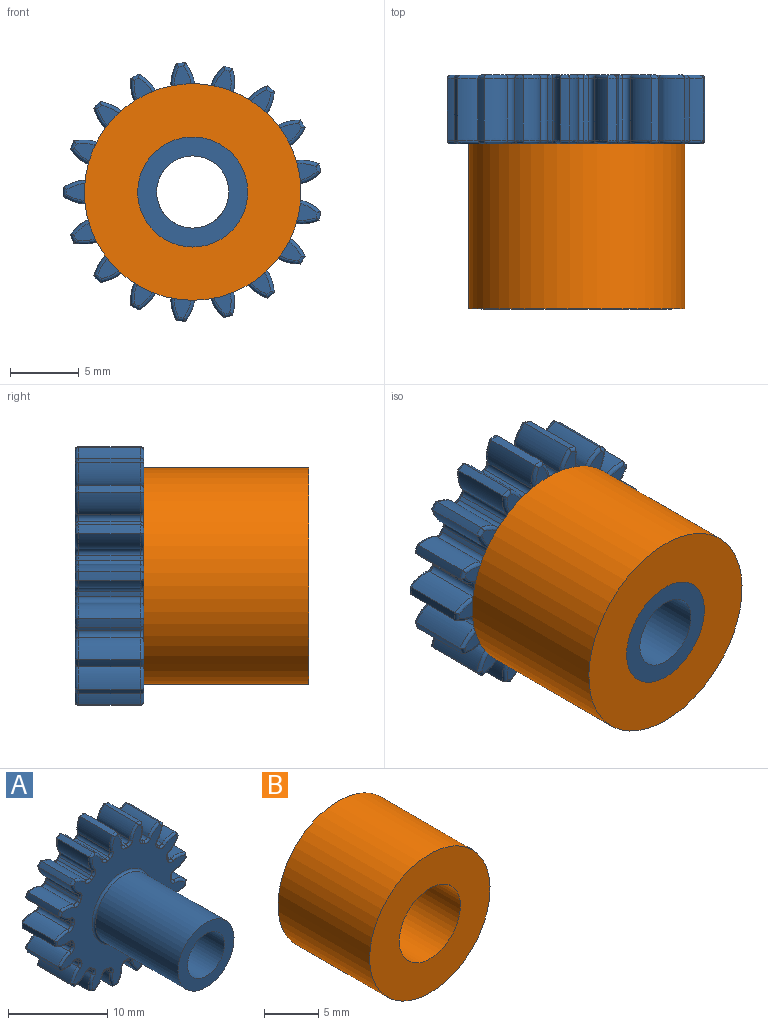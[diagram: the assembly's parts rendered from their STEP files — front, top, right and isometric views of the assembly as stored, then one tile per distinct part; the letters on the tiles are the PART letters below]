
ASSEMBLY  parts=2 mates=1
PART A: 313 faces, bbox 19.3x17x19.3 mm
  f0: cylinder r=9.42mm len=4.5mm, axis (0,1,0), area 3mm2, adj f65,f102,f161,f263
  f1: cylinder r=9.42mm len=4.5mm, axis (0,1,0), area 3mm2, adj f97,f100,f173,f275
  f2: cylinder r=9.42mm len=4.5mm, axis (0,1,0), area 3mm2, adj f85,f92,f197,f299
  f3: cylinder r=9.42mm len=4.5mm, axis (0,1,0), area 3mm2, adj f87,f95,f185,f287
  f4: cylinder r=9.42mm len=4.5mm, axis (0,1,0), area 3mm2, adj f45,f82,f113,f215
  f5: cylinder r=9.42mm len=4.5mm, axis (0,1,0), area 3mm2, adj f77,f80,f125,f227
  f6: cylinder r=9.42mm len=4.5mm, axis (0,1,0), area 3mm2, adj f72,f75,f137,f239
  f7: cylinder r=9.42mm len=4.5mm, axis (0,1,0), area 3mm2, adj f67,f70,f149,f251
  f8: cylinder r=9.42mm len=4.5mm, axis (0,1,0), area 3mm2, adj f25,f62,f150,f252
  f9: cylinder r=9.42mm len=4.5mm, axis (0,1,0), area 3mm2, adj f57,f60,f138,f240
  f10: cylinder r=9.42mm len=4.5mm, axis (0,1,0), area 3mm2, adj f52,f55,f126,f228
  f11: cylinder r=9.42mm len=4.5mm, axis (0,1,0), area 3mm2, adj f47,f50,f114,f216
  f12: cylinder r=9.42mm len=4.5mm, axis (0,1,0), area 3mm2, adj f35,f42,f186,f288
  f13: cylinder r=9.42mm len=4.5mm, axis (0,1,0), area 3mm2, adj f20,f37,f198,f300
  f14: cylinder r=9.42mm len=4.5mm, axis (0,1,0), area 3mm2, adj f32,f40,f174,f276
  f15: cylinder r=9.42mm len=4.5mm, axis (0,1,0), area 3mm2, adj f27,f30,f162,f264
  f16: plane 18.29x18.21mm, normal (0,-1,0), area 134.6mm2, adj f107,f108,f109,f110,f111,f112,f113,f114
  f17: cylinder r=2.62mm len=16.75mm, axis (0,1,0), area 276.3mm2, adj f106,f312
  f18: cylinder r=9.42mm len=4.5mm, axis (0,1,0), area 3mm2, adj f22,f90,f209,f311
  f19: plane 18.29x18.21mm, normal (0,1,0), area 165.4mm2, adj f210,f211,f212,f213,f214,f215,f216,f217
  f20: extruded ~4.5x1.76mm, area 9mm2, adj f13,f23,f200,f302
  f21: cylinder r=7.19mm len=4.5mm, axis (0,1,0), area 1.6mm2, adj f23,f24,f204,f306
  f22: extruded ~4.5x1.76mm, area 9mm2, adj f18,f24,f208,f310
  f23: cylinder r=0.4mm len=4.5mm, axis (0,1,0), area 2.7mm2, adj f20,f21,f202,f304
  f24: cylinder r=0.4mm len=4.5mm, axis (0,1,0), area 2.7mm2, adj f21,f22,f206,f308
  f25: extruded ~4.5x1.82mm, area 9mm2, adj f8,f28,f152,f254
  f26: cylinder r=7.19mm len=4.5mm, axis (0,1,0), area 1.6mm2, adj f28,f29,f156,f258
  f27: extruded ~4.5x1.67mm, area 9mm2, adj f15,f29,f160,f262
  f28: cylinder r=0.4mm len=4.5mm, axis (0,1,0), area 2.7mm2, adj f25,f26,f154,f256
  f29: cylinder r=0.4mm len=4.5mm, axis (0,1,0), area 2.7mm2, adj f26,f27,f158,f260
  f30: extruded ~4.5x1.94mm, area 9mm2, adj f15,f33,f164,f266
  f31: cylinder r=7.19mm len=4.5mm, axis (0,1,0), area 1.6mm2, adj f33,f34,f168,f270
  f32: extruded ~4.5x1.51mm, area 9mm2, adj f14,f34,f172,f274
  f33: cylinder r=0.4mm len=4.5mm, axis (0,1,0), area 2.7mm2, adj f30,f31,f166,f268
  f34: cylinder r=0.4mm len=4.5mm, axis (0,1,0), area 2.7mm2, adj f31,f32,f170,f272
  f35: extruded ~4.5x1.39mm, area 9mm2, adj f12,f38,f188,f290
  f36: cylinder r=7.19mm len=4.5mm, axis (0,1,0), area 1.6mm2, adj f38,f39,f192,f294
  f37: extruded ~4.5x1.93mm, area 9mm2, adj f13,f39,f196,f298
  f38: cylinder r=0.4mm len=4.5mm, axis (0,1,0), area 2.7mm2, adj f35,f36,f190,f292
  f39: cylinder r=0.4mm len=4.5mm, axis (0,1,0), area 2.7mm2, adj f36,f37,f194,f296
  f40: extruded ~4.5x1.79mm, area 9mm2, adj f14,f43,f176,f278
  f41: cylinder r=7.19mm len=4.5mm, axis (0,1,0), area 1.6mm2, adj f43,f44,f180,f282
  f42: extruded ~4.5x1.85mm, area 9mm2, adj f12,f44,f184,f286
  f43: cylinder r=0.4mm len=4.5mm, axis (0,1,0), area 2.7mm2, adj f40,f41,f178,f280
  f44: cylinder r=0.4mm len=4.5mm, axis (0,1,0), area 2.7mm2, adj f41,f42,f182,f284
  f45: extruded ~4.5x1.88mm, area 9mm2, adj f4,f48,f111,f213
  f46: cylinder r=7.19mm len=4.5mm, axis (0,1,0), area 1.6mm2, adj f48,f49,f108,f210
  f47: extruded ~4.5x1.58mm, area 9mm2, adj f11,f49,f112,f214
  f48: cylinder r=0.4mm len=4.5mm, axis (0,1,0), area 2.7mm2, adj f45,f46,f109,f211
  f49: cylinder r=0.4mm len=4.5mm, axis (0,1,0), area 2.7mm2, adj f46,f47,f110,f212
  f50: extruded ~4.5x1.92mm, area 9mm2, adj f11,f53,f116,f218
  f51: cylinder r=7.19mm len=4.5mm, axis (0,1,0), area 1.6mm2, adj f53,f54,f120,f222
  f52: extruded ~4.5x1.62mm, area 9mm2, adj f10,f54,f124,f226
  f53: cylinder r=0.4mm len=4.5mm, axis (0,1,0), area 2.7mm2, adj f50,f51,f118,f220
  f54: cylinder r=0.4mm len=4.5mm, axis (0,1,0), area 2.7mm2, adj f51,f52,f122,f224
  f55: extruded ~4.5x1.71mm, area 9mm2, adj f10,f58,f128,f230
  f56: cylinder r=7.19mm len=4.5mm, axis (0,1,0), area 1.6mm2, adj f58,f59,f132,f234
  f57: extruded ~4.5x1.89mm, area 9mm2, adj f9,f59,f136,f238
  f58: cylinder r=0.4mm len=4.5mm, axis (0,1,0), area 2.7mm2, adj f55,f56,f130,f232
  f59: cylinder r=0.4mm len=4.5mm, axis (0,1,0), area 2.7mm2, adj f56,f57,f134,f236
  f60: extruded ~4.5x1.47mm, area 9mm2, adj f9,f63,f140,f242
  f61: cylinder r=7.19mm len=4.5mm, axis (0,1,0), area 1.6mm2, adj f63,f64,f144,f246
  f62: extruded ~4.5x1.91mm, area 9mm2, adj f8,f64,f148,f250
  f63: cylinder r=0.4mm len=4.5mm, axis (0,1,0), area 2.7mm2, adj f60,f61,f142,f244
  f64: cylinder r=0.4mm len=4.5mm, axis (0,1,0), area 2.7mm2, adj f61,f62,f146,f248
  f65: extruded ~4.5x1.91mm, area 9mm2, adj f0,f68,f159,f261
  f66: cylinder r=7.19mm len=4.5mm, axis (0,1,0), area 1.6mm2, adj f68,f69,f155,f257
  f67: extruded ~4.5x1.47mm, area 9mm2, adj f7,f69,f151,f253
  f68: cylinder r=0.4mm len=4.5mm, axis (0,1,0), area 2.7mm2, adj f65,f66,f157,f259
  f69: cylinder r=0.4mm len=4.5mm, axis (0,1,0), area 2.7mm2, adj f66,f67,f153,f255
  f70: extruded ~4.5x1.89mm, area 9mm2, adj f7,f73,f147,f249
  f71: cylinder r=7.19mm len=4.5mm, axis (0,1,0), area 1.6mm2, adj f73,f74,f143,f245
  f72: extruded ~4.5x1.71mm, area 9mm2, adj f6,f74,f139,f241
  f73: cylinder r=0.4mm len=4.5mm, axis (0,1,0), area 2.7mm2, adj f70,f71,f145,f247
  f74: cylinder r=0.4mm len=4.5mm, axis (0,1,0), area 2.7mm2, adj f71,f72,f141,f243
  f75: extruded ~4.5x1.62mm, area 9mm2, adj f6,f78,f135,f237
  f76: cylinder r=7.19mm len=4.5mm, axis (0,1,0), area 1.6mm2, adj f78,f79,f131,f233
  f77: extruded ~4.5x1.92mm, area 9mm2, adj f5,f79,f127,f229
  f78: cylinder r=0.4mm len=4.5mm, axis (0,1,0), area 2.7mm2, adj f75,f76,f133,f235
  f79: cylinder r=0.4mm len=4.5mm, axis (0,1,0), area 2.7mm2, adj f76,f77,f129,f231
  f80: extruded ~4.5x1.58mm, area 9mm2, adj f5,f83,f123,f225
  f81: cylinder r=7.19mm len=4.5mm, axis (0,1,0), area 1.6mm2, adj f83,f84,f119,f221
  f82: extruded ~4.5x1.88mm, area 9mm2, adj f4,f84,f115,f217
  f83: cylinder r=0.4mm len=4.5mm, axis (0,1,0), area 2.7mm2, adj f80,f81,f121,f223
  f84: cylinder r=0.4mm len=4.5mm, axis (0,1,0), area 2.7mm2, adj f81,f82,f117,f219
  f85: extruded ~4.5x1.85mm, area 9mm2, adj f2,f88,f195,f297
  f86: cylinder r=7.19mm len=4.5mm, axis (0,1,0), area 1.6mm2, adj f88,f89,f191,f293
  f87: extruded ~4.5x1.79mm, area 9mm2, adj f3,f89,f187,f289
  f88: cylinder r=0.4mm len=4.5mm, axis (0,1,0), area 2.7mm2, adj f85,f86,f193,f295
  f89: cylinder r=0.4mm len=4.5mm, axis (0,1,0), area 2.7mm2, adj f86,f87,f189,f291
  f90: extruded ~4.5x1.93mm, area 9mm2, adj f18,f93,f207,f309
  f91: cylinder r=7.19mm len=4.5mm, axis (0,1,0), area 1.6mm2, adj f93,f94,f203,f305
  f92: extruded ~4.5x1.39mm, area 9mm2, adj f2,f94,f199,f301
  f93: cylinder r=0.4mm len=4.5mm, axis (0,1,0), area 2.7mm2, adj f90,f91,f205,f307
  f94: cylinder r=0.4mm len=4.5mm, axis (0,1,0), area 2.7mm2, adj f91,f92,f201,f303
  f95: extruded ~4.5x1.51mm, area 9mm2, adj f3,f98,f183,f285
  f96: cylinder r=7.19mm len=4.5mm, axis (0,1,0), area 1.6mm2, adj f98,f99,f179,f281
  f97: extruded ~4.5x1.94mm, area 9mm2, adj f1,f99,f175,f277
  f98: cylinder r=0.4mm len=4.5mm, axis (0,1,0), area 2.7mm2, adj f95,f96,f181,f283
  f99: cylinder r=0.4mm len=4.5mm, axis (0,1,0), area 2.7mm2, adj f96,f97,f177,f279
  f100: extruded ~4.5x1.67mm, area 9mm2, adj f1,f103,f171,f273
  f101: cylinder r=7.19mm len=4.5mm, axis (0,1,0), area 1.6mm2, adj f103,f104,f167,f269
  f102: extruded ~4.5x1.82mm, area 9mm2, adj f0,f104,f163,f265
  f103: cylinder r=0.4mm len=4.5mm, axis (0,1,0), area 2.7mm2, adj f100,f101,f169,f271
  f104: cylinder r=0.4mm len=4.5mm, axis (0,1,0), area 2.7mm2, adj f101,f102,f165,f267
  f105: cylinder r=4mm len=11.75mm, axis (0,1,0), area 295.3mm2, adj f106,f107
  f106: plane 8x8mm, normal (0,-1,0), area 28.6mm2, adj f17,f105
  f107: torus R=4.25mm, axis (0,-1,0), area 10.1mm2, adj f16,f105
  f108: torus R=6.94mm, axis (0,-1,0), area 0.1mm2, adj f16,f46,f109,f110
  f109: torus R=0.65mm, axis (0,-1,0), area 0.3mm2, adj f16,f48,f108,f111
  f110: torus R=0.65mm, axis (0,-1,0), area 0.3mm2, adj f16,f49,f108,f112
  f111: bspline ~3.83x0.9mm, area 0.7mm2, adj f16,f45,f109,f113
  f112: bspline ~2.24x1.65mm, area 0.7mm2, adj f16,f47,f110,f114
  f113: torus R=9.17mm, axis (0,-1,0), area 0.2mm2, adj f4,f16,f111,f115
  f114: torus R=9.17mm, axis (0,-1,0), area 0.2mm2, adj f11,f16,f112,f116
  f115: bspline ~3.83x0.9mm, area 0.7mm2, adj f16,f82,f113,f117
  f116: bspline ~3.73x1.28mm, area 0.7mm2, adj f16,f50,f114,f118
  f117: torus R=0.65mm, axis (0,-1,0), area 0.3mm2, adj f16,f84,f115,f119
  f118: torus R=0.65mm, axis (0,-1,0), area 0.3mm2, adj f16,f53,f116,f120
  f119: torus R=6.94mm, axis (0,-1,0), area 0.1mm2, adj f16,f81,f117,f121
  f120: torus R=6.94mm, axis (0,-1,0), area 0.1mm2, adj f16,f51,f118,f122
  f121: torus R=0.65mm, axis (0,-1,0), area 0.3mm2, adj f16,f83,f119,f123
  f122: torus R=0.65mm, axis (0,-1,0), area 0.3mm2, adj f16,f54,f120,f124
  f123: bspline ~3.43x1.97mm, area 0.7mm2, adj f16,f80,f121,f125
  f124: bspline ~2.99x2.65mm, area 0.7mm2, adj f16,f52,f122,f126
  f125: torus R=9.17mm, axis (0,-1,0), area 0.2mm2, adj f5,f16,f123,f127
  f126: torus R=9.17mm, axis (0,-1,0), area 0.2mm2, adj f10,f16,f124,f128
  f127: bspline ~3.73x1.28mm, area 0.7mm2, adj f16,f77,f125,f129
  f128: bspline ~3.19x2.39mm, area 0.7mm2, adj f16,f55,f126,f130
  f129: torus R=0.65mm, axis (0,-1,0), area 0.3mm2, adj f16,f79,f127,f131
  f130: torus R=0.65mm, axis (0,-1,0), area 0.3mm2, adj f16,f58,f128,f132
  f131: torus R=6.94mm, axis (0,-1,0), area 0.1mm2, adj f16,f76,f129,f133
  f132: torus R=6.94mm, axis (0,-1,0), area 0.1mm2, adj f16,f56,f130,f134
  f133: torus R=0.65mm, axis (0,-1,0), area 0.3mm2, adj f16,f78,f131,f135
  f134: torus R=0.65mm, axis (0,-1,0), area 0.3mm2, adj f16,f59,f132,f136
  f135: bspline ~2.99x2.65mm, area 0.7mm2, adj f16,f75,f133,f137
  f136: bspline ~3.62x1.52mm, area 0.7mm2, adj f16,f57,f134,f138
  f137: torus R=9.17mm, axis (0,-1,0), area 0.2mm2, adj f6,f16,f135,f139
  f138: torus R=9.17mm, axis (0,-1,0), area 0.2mm2, adj f9,f16,f136,f140
  f139: bspline ~3.19x2.39mm, area 0.7mm2, adj f16,f72,f137,f141
  f140: bspline ~3.27x2.25mm, area 0.7mm2, adj f16,f60,f138,f142
  f141: torus R=0.65mm, axis (0,-1,0), area 0.3mm2, adj f16,f74,f139,f143
  f142: torus R=0.65mm, axis (0,-1,0), area 0.3mm2, adj f16,f63,f140,f144
  f143: torus R=6.94mm, axis (0,-1,0), area 0.1mm2, adj f16,f71,f141,f145
  f144: torus R=6.94mm, axis (0,-1,0), area 0.1mm2, adj f16,f61,f142,f146
  f145: torus R=0.65mm, axis (0,-1,0), area 0.3mm2, adj f16,f73,f143,f147
  f146: torus R=0.65mm, axis (0,-1,0), area 0.3mm2, adj f16,f64,f144,f148
  f147: bspline ~3.62x1.52mm, area 0.7mm2, adj f16,f70,f145,f149
  f148: bspline ~3.85x0.75mm, area 0.7mm2, adj f16,f62,f146,f150
  f149: torus R=9.17mm, axis (0,-1,0), area 0.2mm2, adj f7,f16,f147,f151
  f150: torus R=9.17mm, axis (0,-1,0), area 0.2mm2, adj f8,f16,f148,f152
  f151: bspline ~3.27x2.25mm, area 0.7mm2, adj f16,f67,f149,f153
  f152: bspline ~3.77x1.06mm, area 0.7mm2, adj f16,f25,f150,f154
  f153: torus R=0.65mm, axis (0,-1,0), area 0.3mm2, adj f16,f69,f151,f155
  f154: torus R=0.65mm, axis (0,-1,0), area 0.3mm2, adj f16,f28,f152,f156
  f155: torus R=6.94mm, axis (0,-1,0), area 0.1mm2, adj f16,f66,f153,f157
  f156: torus R=6.94mm, axis (0,-1,0), area 0.1mm2, adj f16,f26,f154,f158
  f157: torus R=0.65mm, axis (0,-1,0), area 0.3mm2, adj f16,f68,f155,f159
  f158: torus R=0.65mm, axis (0,-1,0), area 0.3mm2, adj f16,f29,f156,f160
  f159: bspline ~3.85x0.75mm, area 0.7mm2, adj f16,f65,f157,f161
  f160: bspline ~3.61x1.67mm, area 0.7mm2, adj f16,f27,f158,f162
  f161: torus R=9.17mm, axis (0,-1,0), area 0.2mm2, adj f0,f16,f159,f163
  f162: torus R=9.17mm, axis (0,-1,0), area 0.2mm2, adj f15,f16,f160,f164
  f163: bspline ~3.77x1.06mm, area 0.7mm2, adj f16,f102,f161,f165
  f164: bspline ~3.8x1.06mm, area 0.7mm2, adj f16,f30,f162,f166
  f165: torus R=0.65mm, axis (0,-1,0), area 0.3mm2, adj f16,f104,f163,f167
  f166: torus R=0.65mm, axis (0,-1,0), area 0.3mm2, adj f16,f33,f164,f168
  f167: torus R=6.94mm, axis (0,-1,0), area 0.1mm2, adj f16,f101,f165,f169
  f168: torus R=6.94mm, axis (0,-1,0), area 0.1mm2, adj f16,f31,f166,f170
  f169: torus R=0.65mm, axis (0,-1,0), area 0.3mm2, adj f16,f103,f167,f171
  f170: torus R=0.65mm, axis (0,-1,0), area 0.3mm2, adj f16,f34,f168,f172
  f171: bspline ~3.61x1.67mm, area 0.7mm2, adj f16,f100,f169,f173
  f172: bspline ~2.87x2.76mm, area 0.7mm2, adj f16,f32,f170,f174
  f173: torus R=9.17mm, axis (0,-1,0), area 0.2mm2, adj f1,f16,f171,f175
  f174: torus R=9.17mm, axis (0,-1,0), area 0.2mm2, adj f14,f16,f172,f176
  f175: bspline ~3.8x1.06mm, area 0.7mm2, adj f16,f97,f173,f177
  f176: bspline ~3.35x2.1mm, area 0.7mm2, adj f16,f40,f174,f178
  f177: torus R=0.65mm, axis (0,-1,0), area 0.3mm2, adj f16,f99,f175,f179
  f178: torus R=0.65mm, axis (0,-1,0), area 0.3mm2, adj f16,f43,f176,f180
  f179: torus R=6.94mm, axis (0,-1,0), area 0.1mm2, adj f16,f96,f177,f181
  f180: torus R=6.94mm, axis (0,-1,0), area 0.1mm2, adj f16,f41,f178,f182
  f181: torus R=0.65mm, axis (0,-1,0), area 0.3mm2, adj f16,f98,f179,f183
  f182: torus R=0.65mm, axis (0,-1,0), area 0.3mm2, adj f16,f44,f180,f184
  f183: bspline ~2.87x2.76mm, area 0.7mm2, adj f16,f95,f181,f185
  f184: bspline ~3.48x1.79mm, area 0.7mm2, adj f16,f42,f182,f186
  f185: torus R=9.17mm, axis (0,-1,0), area 0.2mm2, adj f3,f16,f183,f187
  f186: torus R=9.17mm, axis (0,-1,0), area 0.2mm2, adj f12,f16,f184,f188
  f187: bspline ~3.35x2.1mm, area 0.7mm2, adj f16,f87,f185,f189
  f188: bspline ~3.08x2.51mm, area 0.7mm2, adj f16,f35,f186,f190
  f189: torus R=0.65mm, axis (0,-1,0), area 0.3mm2, adj f16,f89,f187,f191
  f190: torus R=0.65mm, axis (0,-1,0), area 0.3mm2, adj f16,f38,f188,f192
  f191: torus R=6.94mm, axis (0,-1,0), area 0.1mm2, adj f16,f86,f189,f193
  f192: torus R=6.94mm, axis (0,-1,0), area 0.1mm2, adj f16,f36,f190,f194
  f193: torus R=0.65mm, axis (0,-1,0), area 0.3mm2, adj f16,f88,f191,f195
  f194: torus R=0.65mm, axis (0,-1,0), area 0.3mm2, adj f16,f39,f192,f196
  f195: bspline ~3.48x1.79mm, area 0.7mm2, adj f16,f85,f193,f197
  f196: bspline ~3.85x0.85mm, area 0.7mm2, adj f16,f37,f194,f198
  f197: torus R=9.17mm, axis (0,-1,0), area 0.2mm2, adj f2,f16,f195,f199
  f198: torus R=9.17mm, axis (0,-1,0), area 0.2mm2, adj f13,f16,f196,f200
  f199: bspline ~3.08x2.51mm, area 0.7mm2, adj f16,f92,f197,f201
  f200: bspline ~3.71x1.35mm, area 0.7mm2, adj f16,f20,f198,f202
  f201: torus R=0.65mm, axis (0,-1,0), area 0.3mm2, adj f16,f94,f199,f203
  f202: torus R=0.65mm, axis (0,-1,0), area 0.3mm2, adj f16,f23,f200,f204
  f203: torus R=6.94mm, axis (0,-1,0), area 0.1mm2, adj f16,f91,f201,f205
  f204: torus R=6.94mm, axis (0,-1,0), area 0.1mm2, adj f16,f21,f202,f206
  f205: torus R=0.65mm, axis (0,-1,0), area 0.3mm2, adj f16,f93,f203,f207
  f206: torus R=0.65mm, axis (0,-1,0), area 0.3mm2, adj f16,f24,f204,f208
  f207: bspline ~3.85x0.85mm, area 0.7mm2, adj f16,f90,f205,f209
  f208: bspline ~3.71x1.35mm, area 0.7mm2, adj f16,f22,f206,f209
  f209: torus R=9.17mm, axis (0,-1,0), area 0.2mm2, adj f16,f18,f207,f208
  f210: torus R=6.94mm, axis (0,-1,0), area 0.1mm2, adj f19,f46,f211,f212
  f211: torus R=0.65mm, axis (0,-1,0), area 0.3mm2, adj f19,f48,f210,f213
  f212: torus R=0.65mm, axis (0,-1,0), area 0.3mm2, adj f19,f49,f210,f214
  f213: bspline ~3.83x0.9mm, area 0.7mm2, adj f19,f45,f211,f215
  f214: bspline ~3.43x1.97mm, area 0.7mm2, adj f19,f47,f212,f216
  f215: torus R=9.17mm, axis (0,-1,0), area 0.2mm2, adj f4,f19,f213,f217
  f216: torus R=9.17mm, axis (0,-1,0), area 0.2mm2, adj f11,f19,f214,f218
  f217: bspline ~3.83x0.9mm, area 0.7mm2, adj f19,f82,f215,f219
  f218: bspline ~3.73x1.28mm, area 0.7mm2, adj f19,f50,f216,f220
  f219: torus R=0.65mm, axis (0,-1,0), area 0.3mm2, adj f19,f84,f217,f221
  f220: torus R=0.65mm, axis (0,-1,0), area 0.3mm2, adj f19,f53,f218,f222
  f221: torus R=6.94mm, axis (0,-1,0), area 0.1mm2, adj f19,f81,f219,f223
  f222: torus R=6.94mm, axis (0,-1,0), area 0.1mm2, adj f19,f51,f220,f224
  f223: torus R=0.65mm, axis (0,-1,0), area 0.3mm2, adj f19,f83,f221,f225
  f224: torus R=0.65mm, axis (0,-1,0), area 0.3mm2, adj f19,f54,f222,f226
  f225: bspline ~3.43x1.97mm, area 0.7mm2, adj f19,f80,f223,f227
  f226: bspline ~2.99x2.65mm, area 0.7mm2, adj f19,f52,f224,f228
  f227: torus R=9.17mm, axis (0,-1,0), area 0.2mm2, adj f5,f19,f225,f229
  f228: torus R=9.17mm, axis (0,-1,0), area 0.2mm2, adj f10,f19,f226,f230
  f229: bspline ~3.73x1.28mm, area 0.7mm2, adj f19,f77,f227,f231
  f230: bspline ~3.19x2.39mm, area 0.7mm2, adj f19,f55,f228,f232
  f231: torus R=0.65mm, axis (0,-1,0), area 0.3mm2, adj f19,f79,f229,f233
  f232: torus R=0.65mm, axis (0,-1,0), area 0.3mm2, adj f19,f58,f230,f234
  f233: torus R=6.94mm, axis (0,-1,0), area 0.1mm2, adj f19,f76,f231,f235
  f234: torus R=6.94mm, axis (0,-1,0), area 0.1mm2, adj f19,f56,f232,f236
  f235: torus R=0.65mm, axis (0,-1,0), area 0.3mm2, adj f19,f78,f233,f237
  f236: torus R=0.65mm, axis (0,-1,0), area 0.3mm2, adj f19,f59,f234,f238
  f237: bspline ~2.99x2.65mm, area 0.7mm2, adj f19,f75,f235,f239
  f238: bspline ~3.62x1.52mm, area 0.7mm2, adj f19,f57,f236,f240
  f239: torus R=9.17mm, axis (0,-1,0), area 0.2mm2, adj f6,f19,f237,f241
  f240: torus R=9.17mm, axis (0,-1,0), area 0.2mm2, adj f9,f19,f238,f242
  f241: bspline ~3.19x2.39mm, area 0.7mm2, adj f19,f72,f239,f243
  f242: bspline ~3.27x2.25mm, area 0.7mm2, adj f19,f60,f240,f244
  f243: torus R=0.65mm, axis (0,-1,0), area 0.3mm2, adj f19,f74,f241,f245
  f244: torus R=0.65mm, axis (0,-1,0), area 0.3mm2, adj f19,f63,f242,f246
  f245: torus R=6.94mm, axis (0,-1,0), area 0.1mm2, adj f19,f71,f243,f247
  f246: torus R=6.94mm, axis (0,-1,0), area 0.1mm2, adj f19,f61,f244,f248
  f247: torus R=0.65mm, axis (0,-1,0), area 0.3mm2, adj f19,f73,f245,f249
  f248: torus R=0.65mm, axis (0,-1,0), area 0.3mm2, adj f19,f64,f246,f250
  f249: bspline ~3.62x1.52mm, area 0.7mm2, adj f19,f70,f247,f251
  f250: bspline ~3.85x0.75mm, area 0.7mm2, adj f19,f62,f248,f252
  f251: torus R=9.17mm, axis (0,-1,0), area 0.2mm2, adj f7,f19,f249,f253
  f252: torus R=9.17mm, axis (0,-1,0), area 0.2mm2, adj f8,f19,f250,f254
  f253: bspline ~3.27x2.25mm, area 0.7mm2, adj f19,f67,f251,f255
  f254: bspline ~3.77x1.06mm, area 0.7mm2, adj f19,f25,f252,f256
  f255: torus R=0.65mm, axis (0,-1,0), area 0.3mm2, adj f19,f69,f253,f257
  f256: torus R=0.65mm, axis (0,-1,0), area 0.3mm2, adj f19,f28,f254,f258
  f257: torus R=6.94mm, axis (0,-1,0), area 0.1mm2, adj f19,f66,f255,f259
  f258: torus R=6.94mm, axis (0,-1,0), area 0.1mm2, adj f19,f26,f256,f260
  f259: torus R=0.65mm, axis (0,-1,0), area 0.3mm2, adj f19,f68,f257,f261
  f260: torus R=0.65mm, axis (0,-1,0), area 0.3mm2, adj f19,f29,f258,f262
  f261: bspline ~3.85x0.75mm, area 0.7mm2, adj f19,f65,f259,f263
  f262: bspline ~3.61x1.67mm, area 0.7mm2, adj f19,f27,f260,f264
  f263: torus R=9.17mm, axis (0,-1,0), area 0.2mm2, adj f0,f19,f261,f265
  f264: torus R=9.17mm, axis (0,-1,0), area 0.2mm2, adj f15,f19,f262,f266
  f265: bspline ~3.77x1.06mm, area 0.7mm2, adj f19,f102,f263,f267
  f266: bspline ~3.8x1.06mm, area 0.7mm2, adj f19,f30,f264,f268
  f267: torus R=0.65mm, axis (0,-1,0), area 0.3mm2, adj f19,f104,f265,f269
  f268: torus R=0.65mm, axis (0,-1,0), area 0.3mm2, adj f19,f33,f266,f270
  f269: torus R=6.94mm, axis (0,-1,0), area 0.1mm2, adj f19,f101,f267,f271
  f270: torus R=6.94mm, axis (0,-1,0), area 0.1mm2, adj f19,f31,f268,f272
  f271: torus R=0.65mm, axis (0,-1,0), area 0.3mm2, adj f19,f103,f269,f273
  f272: torus R=0.65mm, axis (0,-1,0), area 0.3mm2, adj f19,f34,f270,f274
  f273: bspline ~2.36x1.46mm, area 0.7mm2, adj f19,f100,f271,f275
  f274: bspline ~2.87x2.76mm, area 0.7mm2, adj f19,f32,f272,f276
  f275: torus R=9.17mm, axis (0,-1,0), area 0.2mm2, adj f1,f19,f273,f277
  f276: torus R=9.17mm, axis (0,-1,0), area 0.2mm2, adj f14,f19,f274,f278
  f277: bspline ~3.8x1.06mm, area 0.7mm2, adj f19,f97,f275,f279
  f278: bspline ~3.35x2.1mm, area 0.7mm2, adj f19,f40,f276,f280
  f279: torus R=0.65mm, axis (0,-1,0), area 0.3mm2, adj f19,f99,f277,f281
  f280: torus R=0.65mm, axis (0,-1,0), area 0.3mm2, adj f19,f43,f278,f282
  f281: torus R=6.94mm, axis (0,-1,0), area 0.1mm2, adj f19,f96,f279,f283
  f282: torus R=6.94mm, axis (0,-1,0), area 0.1mm2, adj f19,f41,f280,f284
  f283: torus R=0.65mm, axis (0,-1,0), area 0.3mm2, adj f19,f98,f281,f285
  f284: torus R=0.65mm, axis (0,-1,0), area 0.3mm2, adj f19,f44,f282,f286
  f285: bspline ~2.87x2.76mm, area 0.7mm2, adj f19,f95,f283,f287
  f286: bspline ~3.48x1.79mm, area 0.7mm2, adj f19,f42,f284,f288
  f287: torus R=9.17mm, axis (0,-1,0), area 0.2mm2, adj f3,f19,f285,f289
  f288: torus R=9.17mm, axis (0,-1,0), area 0.2mm2, adj f12,f19,f286,f290
  f289: bspline ~3.35x2.1mm, area 0.7mm2, adj f19,f87,f287,f291
  f290: bspline ~3.08x2.51mm, area 0.7mm2, adj f19,f35,f288,f292
  f291: torus R=0.65mm, axis (0,-1,0), area 0.3mm2, adj f19,f89,f289,f293
  f292: torus R=0.65mm, axis (0,-1,0), area 0.3mm2, adj f19,f38,f290,f294
  f293: torus R=6.94mm, axis (0,-1,0), area 0.1mm2, adj f19,f86,f291,f295
  f294: torus R=6.94mm, axis (0,-1,0), area 0.1mm2, adj f19,f36,f292,f296
  f295: torus R=0.65mm, axis (0,-1,0), area 0.3mm2, adj f19,f88,f293,f297
  f296: torus R=0.65mm, axis (0,-1,0), area 0.3mm2, adj f19,f39,f294,f298
  f297: bspline ~3.48x1.79mm, area 0.7mm2, adj f19,f85,f295,f299
  f298: bspline ~3.85x0.85mm, area 0.7mm2, adj f19,f37,f296,f300
  f299: torus R=9.17mm, axis (0,-1,0), area 0.2mm2, adj f2,f19,f297,f301
  f300: torus R=9.17mm, axis (0,-1,0), area 0.2mm2, adj f13,f19,f298,f302
  f301: bspline ~3.08x2.51mm, area 0.7mm2, adj f19,f92,f299,f303
  f302: bspline ~3.71x1.35mm, area 0.7mm2, adj f19,f20,f300,f304
  f303: torus R=0.65mm, axis (0,-1,0), area 0.3mm2, adj f19,f94,f301,f305
  f304: torus R=0.65mm, axis (0,-1,0), area 0.3mm2, adj f19,f23,f302,f306
  f305: torus R=6.94mm, axis (0,-1,0), area 0.1mm2, adj f19,f91,f303,f307
  f306: torus R=6.94mm, axis (0,-1,0), area 0.1mm2, adj f19,f21,f304,f308
  f307: torus R=0.65mm, axis (0,-1,0), area 0.3mm2, adj f19,f93,f305,f309
  f308: torus R=0.65mm, axis (0,-1,0), area 0.3mm2, adj f19,f24,f306,f310
  f309: bspline ~3.85x0.85mm, area 0.7mm2, adj f19,f90,f307,f311
  f310: bspline ~3.71x1.35mm, area 0.7mm2, adj f19,f22,f308,f311
  f311: torus R=9.17mm, axis (0,-1,0), area 0.2mm2, adj f18,f19,f309,f310
  f312: torus R=2.88mm, axis (0,-1,0), area 6.7mm2, adj f17,f19
PART B: 4 faces, bbox 15.8x12x15.8 mm
  f0: cylinder r=7.88mm len=15.75mm, axis (0,1,0), area 593.8mm2, adj f2,f3
  f1: cylinder r=4mm len=12mm, axis (0,1,0), area 301.6mm2, adj f2,f3
  f2: plane 15.75x15.75mm, normal (0,-1,0), area 144.6mm2, adj f0,f1
  f3: plane 15.75x15.75mm, normal (0,1,0), area 144.6mm2, adj f0,f1
PLACE A at identity fixed
PLACE B at identity
MATE fastened B.f1 <-> A.f105  axis (0,1,0) through (0,-5,0)mm
